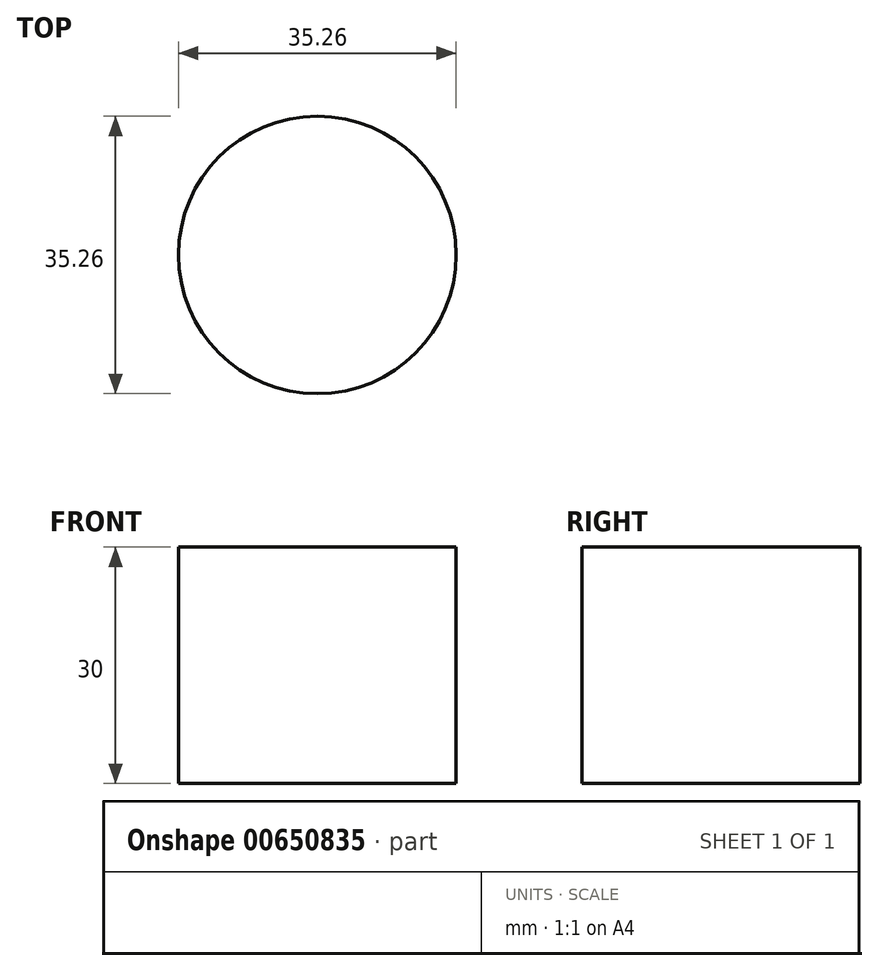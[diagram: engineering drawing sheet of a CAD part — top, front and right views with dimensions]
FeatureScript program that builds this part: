
annotation { "Feature Type Name" : "Feature", "Feature Type Description" : "" }
export const myFeature = defineFeature(function(context is Context, id is Id, definition is map)
    precondition{}
    {
        {
            var Q0;
            Q0=qCreatedBy(makeId("Top.planeOp"),FACE);
            var sketch = newSketch(context, id + "F0", { "sketchPlane" : qUnion([Q0])});
            skCircle(sketch, "E0", {"center": v(0, 0) * mm, "radius": 17.63 * mm});
            skSolve(sketch);
        }
        {
            var Q0;
            Q0 = qSketchRegion(id + "F0", true);
            extrude(context, id + "F1", {"entities" : qUnion([Q0]), "depth" : 30 * mm, "offsetDistance" : 25 * mm});
        }
        {
            var Q0;
            Q0=makeQuery(id+"F1.opExtrude","CAP_FACE",FACE,{"disambiguationData":[OSD([sQuery(id+"F0.wireOp",EDGE,"E0")])],"isStart":false});
            var sketch = newSketch(context, id + "F2", { "sketchPlane" : qUnion([Q0])});
            skLineSegment(sketch, "E1", {"start": v(0, 0) * mm, "end": v(17.63, 0) * mm});
            skSolve(sketch);
        }
        {
            var Q0;
            Q0=qCreatedBy(makeId("Front.planeOp"),FACE);
            var sketch = newSketch(context, id + "F3", { "sketchPlane" : qUnion([Q0])});
            skArc(sketch, "E2", {"start": v(0, 47.64) * mm, "mid": v(12.43, 42.51) * mm, "end": v(17.62, 30.11) * mm});
            skSolve(sketch);
        }
        {
            var Q0;
            Q0=qCreatedBy(makeId("Front.planeOp"),FACE);
            var sketch = newSketch(context, id + "F4", { "sketchPlane" : qUnion([Q0])});
            skLineSegment(sketch, "E3", {"start": v(0, 47.57) * mm, "end": v(0, 29.78) * mm});
            skSolve(sketch);
        }
        {
            var Q0;
            Q0 = qSketchRegion(id + "F3", true);
            var Q1;
            Q1 = qSketchRegion(id + "F4", true);
            var Q2;
            Q2 = qSketchRegion(id + "F2", true);
            var Q3;
            Q3=sQuery(id+"F3.wireOp",EDGE,"E2");
            var Q4;
            Q4=sQuery(id+"F4.wireOp",EDGE,"E3");
            revolve(context, id + "F5", {"bodyType" : ToolBodyType.SURFACE, "entities" : qUnion([Q0, Q1, Q2]), "surfaceEntities" : qUnion([Q3]), "axis" : qUnion([Q4]), "revolveType" : RevolveType.FULL});
        }
        {
            var Q0;
            Q0=qCreatedBy(makeId("Right.planeOp"),FACE);
            var sketch = newSketch(context, id + "F6", { "sketchPlane" : qUnion([Q0])});
            skCircle(sketch, "E4", {"center": v(0, 15.7) * mm, "radius": 0.72 * mm});
            skSolve(sketch);
        }
        {
            var Q0;
            Q0=sQuery(id+"F6.wireOp",EDGE,"E4");
            extrude(context, id + "F7", {"bodyType" : ToolBodyType.SURFACE, "surfaceEntities" : qUnion([Q0]), "depth" : 70 * mm, "offsetDistance" : 25 * mm});
        }
        {
            var Q0;
            Q0=qCreatedBy(makeId("Top.planeOp"),FACE);
            var sketch = newSketch(context, id + "F8", { "sketchPlane" : qUnion([Q0])});
            skCircle(sketch, "E5", {"center": v(67.86, 0) * mm, "radius": 0.55 * mm});
            skSolve(sketch);
        }
        {
            var Q0;
            Q0=sQuery(id+"F8.wireOp",EDGE,"E5");
            extrude(context, id + "F9", {"bodyType" : ToolBodyType.SURFACE, "surfaceEntities" : qUnion([Q0]), "depth" : 20 * mm, "offsetDistance" : 25 * mm});
        }
    });
